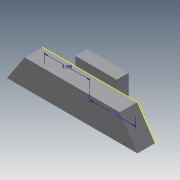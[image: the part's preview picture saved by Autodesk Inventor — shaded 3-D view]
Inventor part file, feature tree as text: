
AUTODESK INVENTOR PART (.ipt)
format: ipt  version: 2011 (Build 150239000, 239)  size: 116,224 bytes
history: native  units: in
note: dims shown in document units (in); Inventor stores cm internally (conversion verified against a paired STEP export)
features: sketch x5, extrude x4
ambient origin geometry x8: Origin, YZ Plane, XZ Plane, XY Plane, X Axis, Y Axis, Z Axis, Center Point
bodies: Solid1 (feature_tree)
feature tree (9):
  extrude  "Extrusion1"  Depth=2.25in
  extrude  "Extrusion2"  Depth=8.0in
  extrude  "Extrusion3"  Depth=0.75in
  extrude  "Extrusion4"  Depth=1.75in
  sketch  "Sketch5"  dims[d10=1.375in d11=3.5in d12=2.75in d13=1.0in d14=0.0in d15=0.5in d16=0.5in d17=0.5in d18=0.75in d19=0.75in d20=2.5in d21=0.1in d22=0.0in d23=3.8583in d24=3.8583in]
  sketch  "Sketch1"  dims[d0=11.0in d1=2.25in]
  sketch  "Sketch2"  dims[d2=4.0in d3=8.0in]
  sketch  "Sketch3"  dims[d4=1.5in d5=0.0in d6=0.75in]
  sketch  "Sketch4"  dims[d7=0.5in d8=0.0in d9=1.75in]
